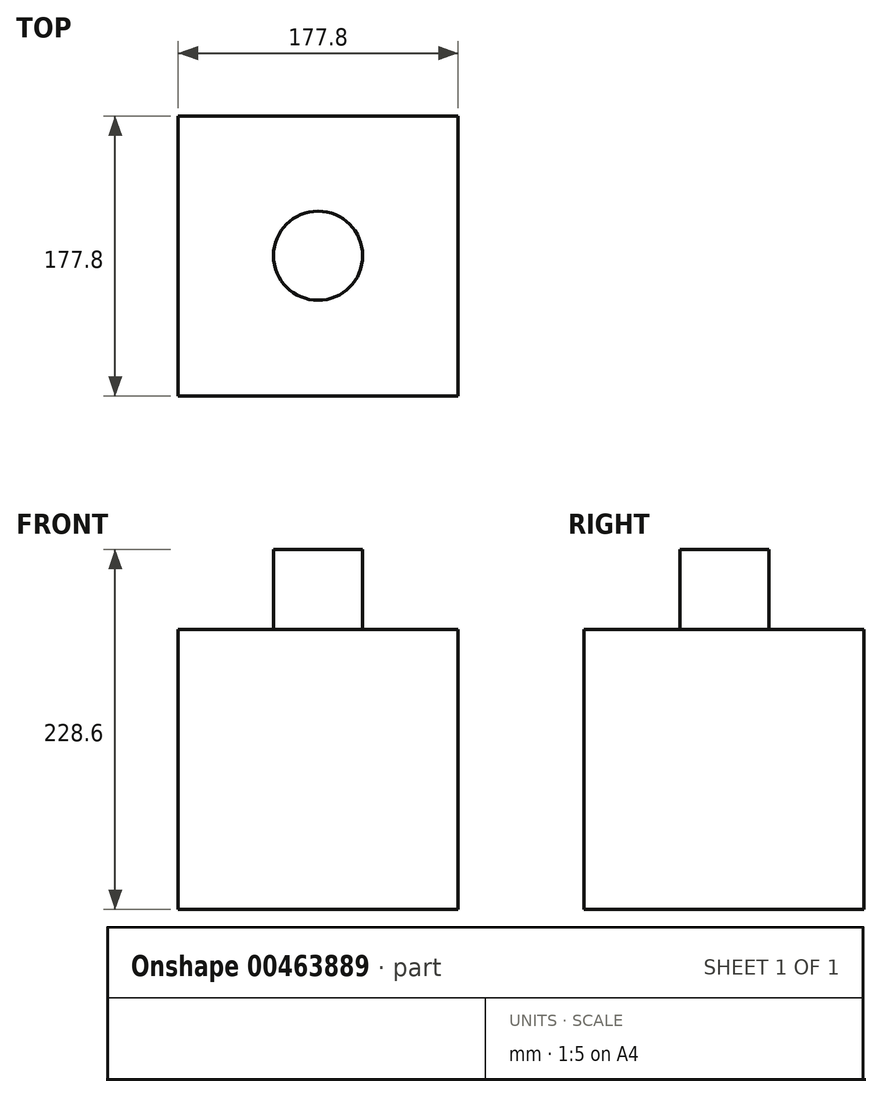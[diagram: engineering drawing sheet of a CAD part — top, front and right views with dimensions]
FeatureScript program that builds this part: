
annotation { "Feature Type Name" : "Feature", "Feature Type Description" : "" }
export const myFeature = defineFeature(function(context is Context, id is Id, definition is map)
    precondition{}
    {
        {
            var Q0;
            Q0=qCreatedBy(makeId("Front.planeOp"),FACE);
            var sketch = newSketch(context, id + "F0", { "sketchPlane" : qUnion([Q0])});
            skLineSegment(sketch, "E0.bottom", {"start": v(-74.73, 92.31) * mm, "end": v(103.07, 92.31) * mm});
            skLineSegment(sketch, "E0.top", {"start": v(-74.73, -85.49) * mm, "end": v(103.07, -85.49) * mm});
            skLineSegment(sketch, "E0.left", {"start": v(-74.73, 92.31) * mm, "end": v(-74.73, -85.49) * mm});
            skLineSegment(sketch, "E0.right", {"start": v(103.07, 92.31) * mm, "end": v(103.07, -85.49) * mm});
            skSolve(sketch);
        }
        {
            var Q0;
            Q0=makeQuery(id+"F0.imprint","IMPRINT",FACE,{"disambiguationData":[TD([[makeQuery(id+"F0.imprint","IMPRINT",EDGE,{"derivedFrom":sQuery(id+"F0.wireOp",EDGE,"E0.bottom")}),-1.0]])]});
            extrude(context, id + "F1", {"entities" : qUnion([Q0]), "depth" : 177.8 * mm});
        }
        {
            var Q0;
            Q0=makeQuery(id+"F1.opExtrude","SWEPT_FACE",FACE,{"disambiguationData":[OSD([sQuery(id+"F0.wireOp",EDGE,"E0.bottom")])]});
            var sketch = newSketch(context, id + "F2", { "sketchPlane" : qUnion([Q0])});
            skPoint(sketch, "E1", {"position": v(14.17, -88.9) * mm});
            skSolve(sketch);
        }
        {
            var Q0;
            {var subQ0=sQuery(id+"F0.wireOp",EDGE,"E0.bottom");Q0=makeQuery(id+"F2.imprint","IMPRINT",FACE,{"disambiguationData":[TD([[makeQuery(id+"F2.imprint","IMPRINT",EDGE,{"derivedFrom":makeQuery(id+"F1.opExtrude","CAP_EDGE",EDGE,{"disambiguationData":[OSD([subQ0])],"isStart":true})}),-1.0]])]});}
            var sketch = newSketch(context, id + "F3", { "sketchPlane" : qUnion([Q0])});
            skCircle(sketch, "E2", {"center": v(14.13, -88.69) * mm, "radius": 28.3 * mm});
            skSolve(sketch);
        }
        {
            var Q0;
            Q0=makeQuery(id+"F3.imprint","IMPRINT",FACE,{"disambiguationData":[TD([[makeQuery(id+"F3.imprint","IMPRINT",EDGE,{"derivedFrom":sQuery(id+"F3.wireOp",EDGE,"E2")}),1.0]])]});
            extrude(context, id + "F4", {"entities" : qUnion([Q0]), "operationType" : NewBodyOperationType.ADD, "depth" : 50.8 * mm});
        }
    });
